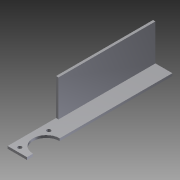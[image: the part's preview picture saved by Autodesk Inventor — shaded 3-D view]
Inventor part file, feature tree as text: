
AUTODESK INVENTOR PART (.ipt)
format: ipt  version: 2012 (Build 160160000, 160)  size: 86,528 bytes
history: native  units: in
note: dims shown in document units (in); Inventor stores cm internally (conversion verified against a paired STEP export)
features: other x3, sketch x2
ambient origin geometry x8: Origin, YZ Plane, XZ Plane, XY Plane, X Axis, Y Axis, Z Axis, Center Point
bodies: Solid1 (feature_tree)
feature tree (5):
  other  "8 ball corner L_MIR.ipt"
  other  "Solid1::8 ball corner L_MIR.ipt"
  sketch  "Sketch1"  dims[d0=0.3937in]
  sketch  "Sketch2"
  other  "TaggingFeature1"
